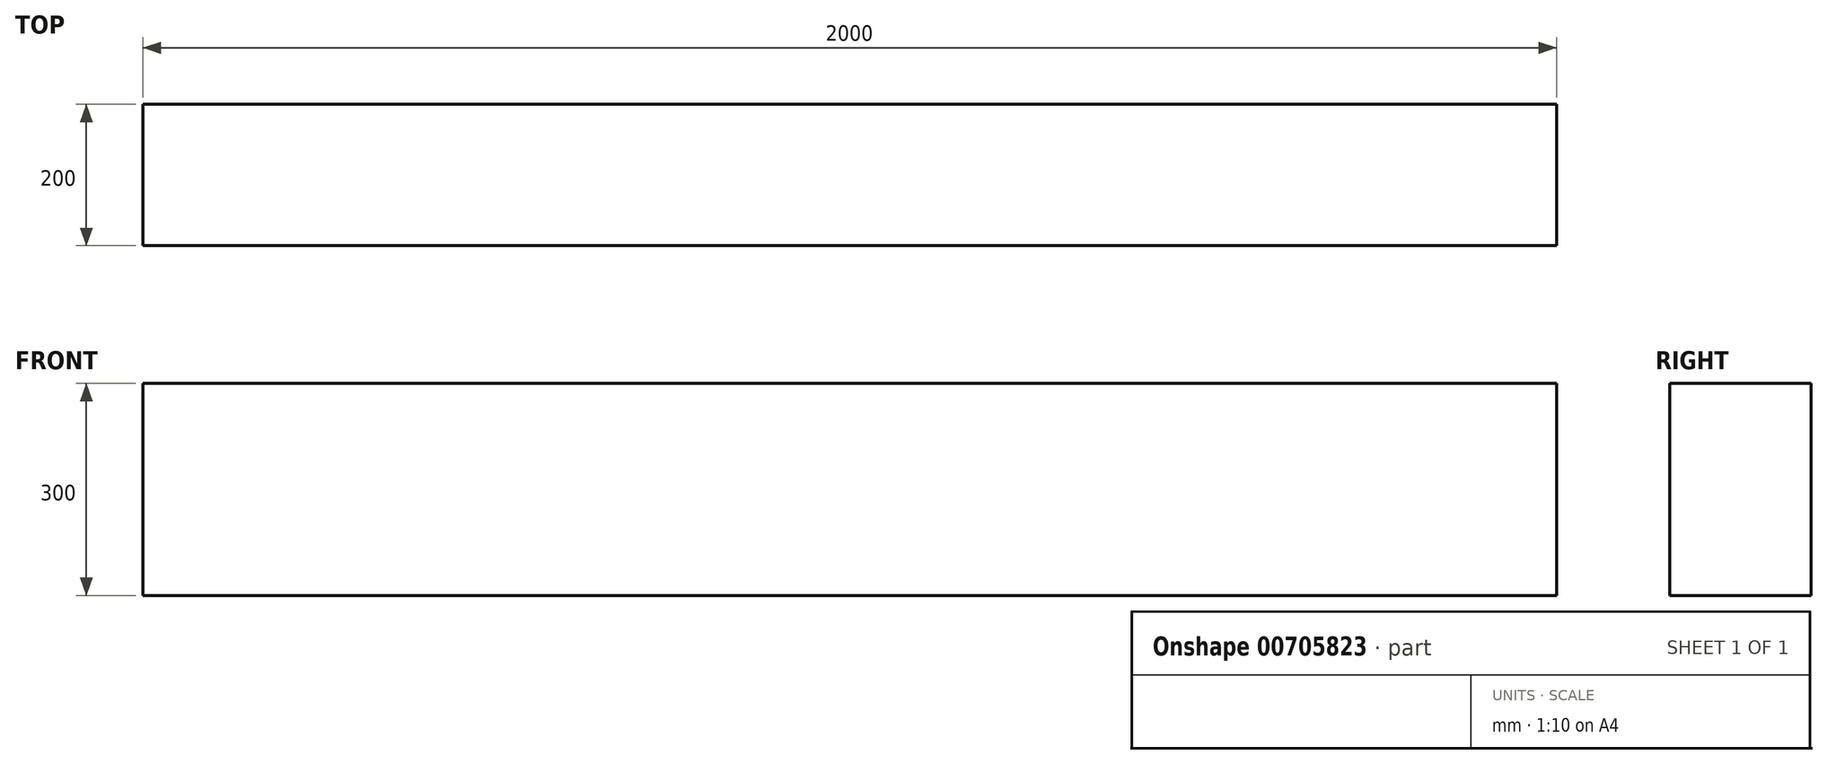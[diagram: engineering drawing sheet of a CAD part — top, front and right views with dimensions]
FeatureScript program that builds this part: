
annotation { "Feature Type Name" : "Feature", "Feature Type Description" : "" }
export const myFeature = defineFeature(function(context is Context, id is Id, definition is map)
    precondition{}
    {
        {
            var Q0;
            Q0=qCreatedBy(makeId("Right.planeOp"),FACE);
            var sketch = newSketch(context, id + "F0", { "sketchPlane" : qUnion([Q0])});
            skLineSegment(sketch, "E0.bottom", {"start": v(-207.36, 259.79) * mm, "end": v(-7.36, 259.79) * mm});
            skLineSegment(sketch, "E0.top", {"start": v(-207.36, -40.21) * mm, "end": v(-7.36, -40.21) * mm});
            skLineSegment(sketch, "E0.left", {"start": v(-207.36, 259.79) * mm, "end": v(-207.36, -40.21) * mm});
            skLineSegment(sketch, "E0.right", {"start": v(-7.36, 259.79) * mm, "end": v(-7.36, -40.21) * mm});
            skSolve(sketch);
        }
        {
            var Q0;
            Q0=makeQuery(id+"F0.imprint","IMPRINT",FACE,{"disambiguationData":[TD([[makeQuery(id+"F0.imprint","IMPRINT",EDGE,{"derivedFrom":sQuery(id+"F0.wireOp",EDGE,"E0.bottom")}),-1.0]])]});
            extrude(context, id + "F1", {"entities" : qUnion([Q0]), "depth" : 2000 * mm, "offsetDistance" : 25 * mm});
        }
    });
